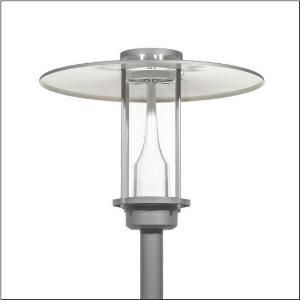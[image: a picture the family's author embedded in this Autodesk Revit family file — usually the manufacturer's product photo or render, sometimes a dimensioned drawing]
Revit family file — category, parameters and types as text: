
# Revit family: city-light_plus_iq___st1_2a_5xa5275af14hp_3410
name_source: partatom
category: Lighting Fixtures
units: mm (PartAtom-declared; Revit-internal decimal feet)

## family parameters
Cut with Voids When Loaded = No
Host = Face
Light Source = No
Part Type = Normal
Room Calculation Point = No
Round Connector Dimension = Use Diameter
Shared = No

## types (1)
- --- (1 x LED, 3730 lm, 33.6 W, 2200K)
    Apparent Load = 34 VA
    CIE Flux Codes = 22 60 93 97 100
    Color Rendering = 70
    Color Temperature = 2200K
    Default Elevation = 1800 mm
    Description = City-Light Plus iQ, mast luminaire, Module 540 iQ-SR, primary light control with 3 zone facetted reflector, of plastic, silver coated, highly specular, structured, primary optical cover: cover, of PMMA, transparent, light distribution: ST1.2a, light emission: direct distribution, primary light characteristic: asymmetric, installation type: post-top, LED, High Power LED, rated luminous flux: 3.730lm, luminous efficacy: 111lm/W, light colour: 722, colour temperature: 2200K, control gear: ECG iQ, control: pre-setting: logarithmic dimming characteristic, Street-Remote, Auto-Match, Temp-Guard, Lumen-Switch, Night-Set, Smart-Wire, Light-Fading, Desk-Remote (wireless, voltage-free reading and setting of iQ features in the workshop via application-optimized NFC function/RFID function), optimised constant luminous flux control (CLO 2.0), with terminal, 6-pole, max. 2.5mm², mains connection: 230..240V, AC, 50/60Hz, start of lifetime: 34W, end of service life: 36W, reduction: 15W, luminaire housing, upper part, of glass-fibre reinforced polyester, coated, Siteco® metallic grey (DB 702S), diameter: 750mm, height: 590mm, spigot size: d x l = 76 x 70mm (post-top) | with reducer (optional accessory) 60 x 70mm, post-top mast mounting element, of diecast aluminium, coated, Siteco® metallic grey (DB 702S), Module 540 iQ-SR, traffic white (RAL 9016), equipment: Power, protection rating (complete): IP65, insulation class (complete): insulation class II (safety insulation), certification: CE, ENEC, VDE, packaging unit: 1 piece

Light Distribution: ST1.2a
    Height = 590 mm
    Lamp = 1 x LED
    Lamp Light Flux = 3730 lm
    Lamp Power = 33.6 W
    Lamp count = 1
    Length = 750 mm
    Luminous efficacy = 111 lm/W
    Manufacturer = Siteco
    ModVariant = No
    Model = 5XA5275AF14HP
    Number of Poles = 1
    OnlyDefault = Yes
    Power Factor = 1
    Product Name = City-Light Plus iQ | ST1.2a
    Product group = mast luminaire | pylon top
    ProductGroupID = 6100
    Protection Class = Protection class II
    Protection Degree = IP 65
    RLX_Detail_Level = 1
    RLX_Emergency_Light_Flux = 0 lm
    RLX_Emergency_Type = 0
    RLX_Emergency_Type_DB = No
    RlxData = <blob elided: 52469 chars, md5=4f4e3081>
    Socket = socket
    Standby Power = 0 W
    System Light Flux = 3730 lm
    System Power = 34 W
    Type Comments = factory setting: luminous flux: 100 % | dim-lin: 254 | 695 mA
    Type Image = l_1006456.jpg
    URL = http://relux.com
    VarID = @adj_166571
    Voltage = 0 V
    Weight = 0.00 kg
    Width = 0 mm  [stored 0 ft]

note: [stored X ft] marks values corroborated as IEEE doubles in the binary element streams (Revit-internal decimal feet)

## geometry (parser evidence)
native form markers: Blend x4, Sweep x12
no freeform markers — native parametric forms only
